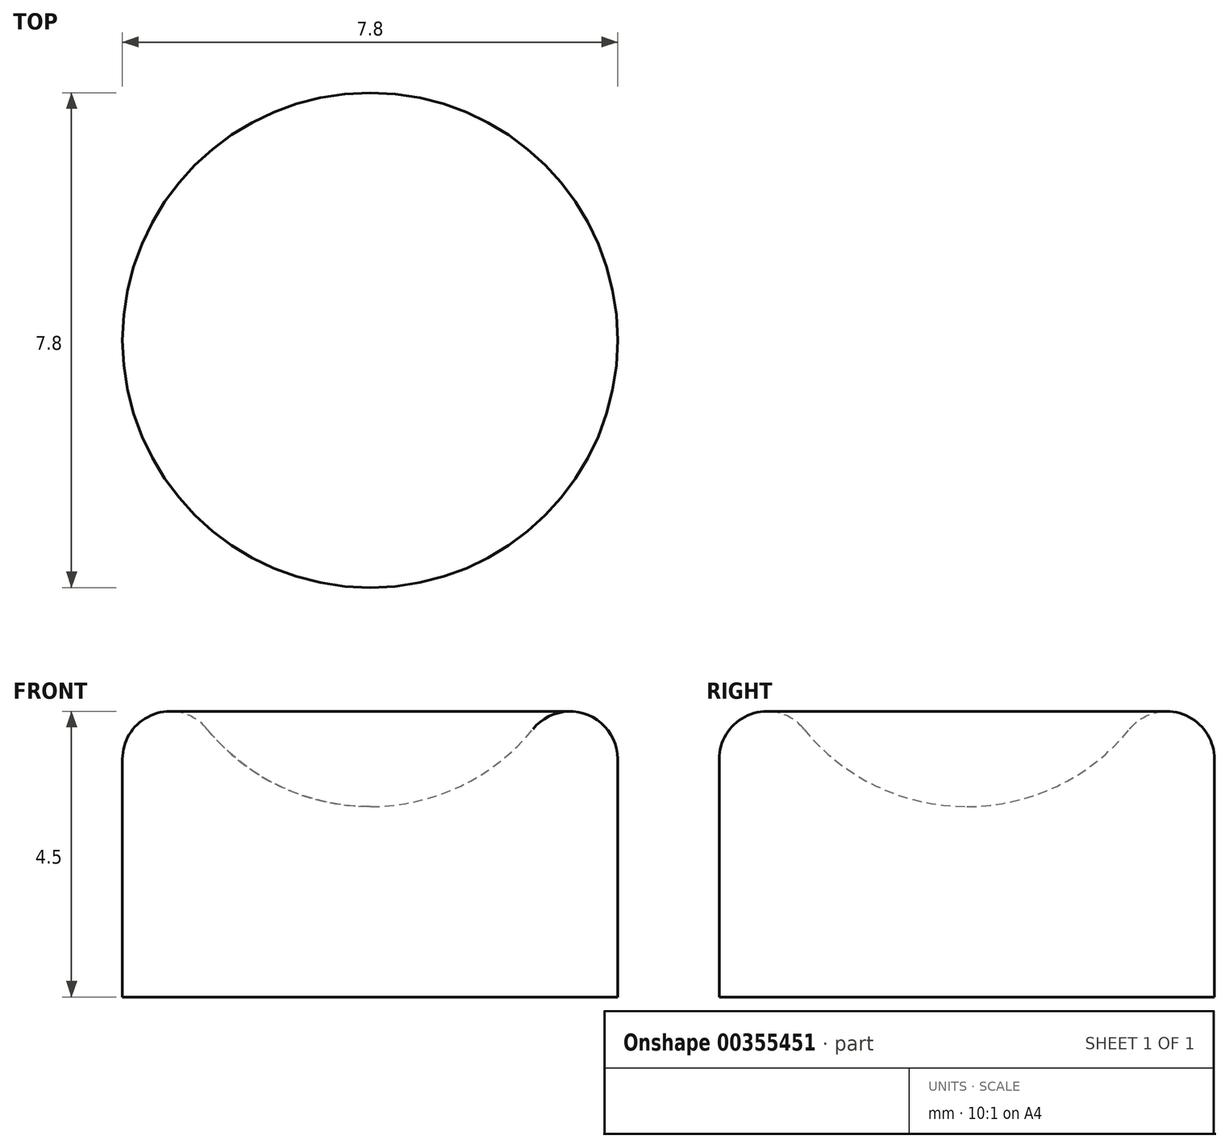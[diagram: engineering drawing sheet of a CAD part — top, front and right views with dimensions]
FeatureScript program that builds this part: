
annotation { "Feature Type Name" : "Feature", "Feature Type Description" : "" }
export const myFeature = defineFeature(function(context is Context, id is Id, definition is map)
    precondition{}
    {
        {
            var Q0;
            Q0=qCreatedBy(makeId("Front.planeOp"),FACE);
            var sketch = newSketch(context, id + "F0", { "sketchPlane" : qUnion([Q0])});
            skLineSegment(sketch, "E0", {"start": v(0, 0) * mm, "end": v(3.9, 0) * mm});
            skLineSegment(sketch, "E1", {"start": v(3.9, 0) * mm, "end": v(3.9, 3.75) * mm});
            skArc(sketch, "E2", {"start": v(3.9, 3.75) * mm, "mid": v(3.4, 4.46) * mm, "end": v(2.57, 4.22) * mm});
            skArc(sketch, "E3", {"start": v(0, 3) * mm, "mid": v(1.42, 3.32) * mm, "end": v(2.57, 4.22) * mm});
            skLineSegment(sketch, "E4", {"start": v(0, 3) * mm, "end": v(0, 0) * mm});
            skLineSegment(sketch, "E5", {"start": v(3.15, 3.75) * mm, "end": v(3.15, 4.5) * mm, "construction": true});
            skSolve(sketch);
        }
        {
            var Q0;
            Q0=makeQuery(id+"F0.imprint","IMPRINT",FACE,{"disambiguationData":[TD([[makeQuery(id+"F0.imprint","IMPRINT",EDGE,{"derivedFrom":sQuery(id+"F0.wireOp",EDGE,"E0")}),1.0]])]});
            var Q1;
            Q1=sQuery(id+"F0.wireOp",EDGE,"E4");
            revolve(context, id + "F1", {"entities" : qUnion([Q0]), "axis" : qUnion([Q1]), "revolveType" : RevolveType.FULL});
        }
    });
